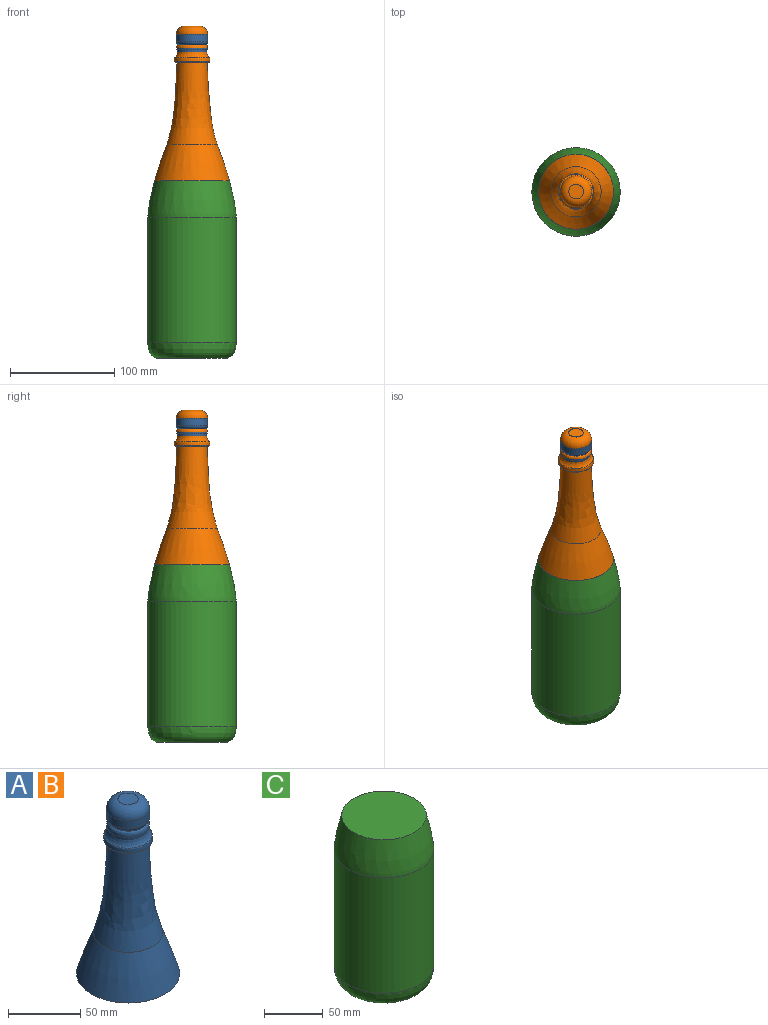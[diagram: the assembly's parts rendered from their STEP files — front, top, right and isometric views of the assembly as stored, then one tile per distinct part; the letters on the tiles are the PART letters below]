
ASSEMBLY  parts=3 mates=1
PART A: 13 faces, bbox 71.6x71.6x148 mm
  f0: plane 14x14mm, normal (0,0,1), area 153.9mm2, adj f12
  f1: plane 71.64x71.64mm, normal (0,0,-1), area 4030.8mm2, adj f2
  f2: revolved ~71.64x71.64mm, area 6957.8mm2, adj f1,f3
  f3: revolved ~78.65x48.06mm, area 8746.2mm2, adj f2,f4
  f4: revolved ~34.01x34.01mm, area 300.7mm2, adj f3,f5
  f5: revolved ~34.01x34.01mm, area 413.8mm2, adj f4,f6
  f6: revolved ~32.9x32.9mm, area 749.3mm2, adj f5,f7
  f7: revolved ~29.65x29.65mm, area 79.4mm2, adj f6,f8
  f8: revolved ~29.76x29.76mm, area 467mm2, adj f7,f9
  f9: torus R=16.76mm, axis (0,0,1), area 80.5mm2, adj f8,f10
  f10: torus R=12mm, axis (0,0,1), area 411.9mm2, adj f9,f11
  f11: cylinder r=15mm len=30mm, axis (0,0,1), area 659.7mm2, adj f10,f12
  f12: torus R=7mm, axis (0,0,1), area 954.8mm2, adj f0,f11
PART B: same geometry as A
PART C: 6 faces, bbox 84.6x84.6x170 mm
  f0: revolved ~67.88x67.88mm, area 3619mm2, adj f1,f5
  f1: cone r=0.02mm half-angle=89.9deg, axis (0,0,-1), area 0mm2, adj f0
  f2: plane 71.68x71.68mm, normal (0,0,1), area 4035.7mm2, adj f3
  f3: revolved ~84.6x84.6mm, area 8874.1mm2, adj f2,f4
  f4: revolved ~119.87x84.6mm, area 31806.1mm2, adj f3,f5
  f5: revolved ~84.6x84.6mm, area 4710.4mm2, adj f0,f4
PLACE A rot(axis=(0,1,0),0deg) t=(0.01,0,-156.82)mm
PLACE B rot(axis=(0,1,0),0deg) t=(0.01,0,-156.79)mm
PLACE C t=(0,0,-156.75)mm
MATE slider B.f9 <-> C.f1  axis (0,0,-1) through (0,0,13.25)mm
